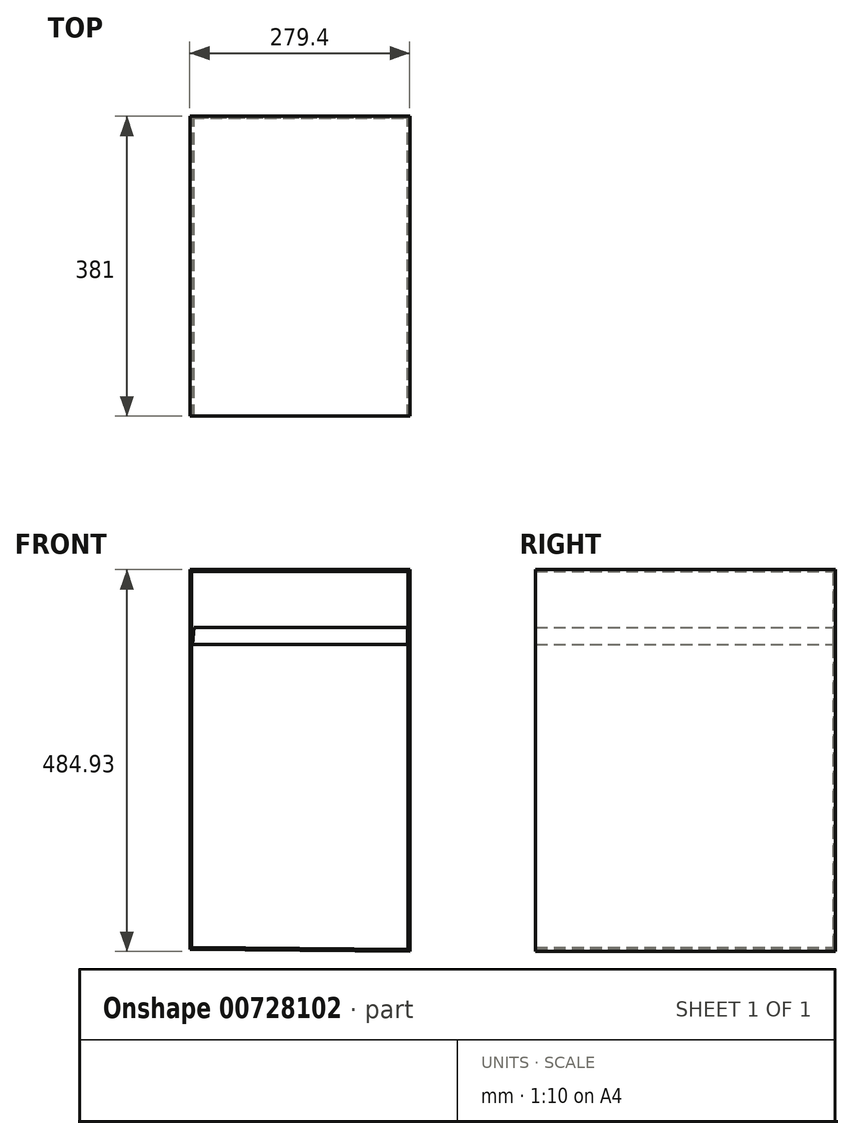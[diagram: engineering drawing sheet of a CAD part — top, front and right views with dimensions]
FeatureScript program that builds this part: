
annotation { "Feature Type Name" : "Feature", "Feature Type Description" : "" }
export const myFeature = defineFeature(function(context is Context, id is Id, definition is map)
    precondition{}
    {
        {
            var Q0;
            Q0=qCreatedBy(makeId("Front.planeOp"),FACE);
            var sketch = newSketch(context, id + "F0", { "sketchPlane" : qUnion([Q0])});
            skLineSegment(sketch, "E0", {"start": v(-49.26, 70.55) * mm, "end": v(-49.26, 553.15) * mm});
            skLineSegment(sketch, "E1", {"start": v(-49.26, 553.15) * mm, "end": v(230.14, 553.15) * mm});
            skLineSegment(sketch, "E2", {"start": v(230.14, 553.15) * mm, "end": v(230.14, 68.22) * mm});
            skLineSegment(sketch, "E3", {"start": v(230.14, 68.22) * mm, "end": v(-49.26, 70.55) * mm});
            skSolve(sketch);
        }
        {
            var Q0;
            Q0 = qSketchRegion(id + "F0", true);
            extrude(context, id + "F1", {"entities" : qUnion([Q0]), "depth" : 381 * mm, "offsetDistance" : 25.4 * mm});
        }
        {
            var Q0;
            Q0=makeQuery(id+"F1.opExtrude","CAP_FACE",FACE,{"disambiguationData":[OSD([sQuery(id+"F0.wireOp",EDGE,"E0"),sQuery(id+"F0.wireOp",EDGE,"E1"),sQuery(id+"F0.wireOp",EDGE,"E2"),sQuery(id+"F0.wireOp",EDGE,"E3")])],"isStart":false});
            shell(context, id + "F2", {"entities" : qUnion([Q0]), "thickness" : 2.54 * mm});
        }
        {
            var Q0;
            Q0=qCreatedBy(makeId("Front.planeOp"),FACE);
            var sketch = newSketch(context, id + "F3", { "sketchPlane" : qUnion([Q0])});
            skLineSegment(sketch, "E4", {"start": v(-43.76, 479.93) * mm, "end": v(227.3, 479.93) * mm});
            skLineSegment(sketch, "E5", {"start": v(227.3, 479.93) * mm, "end": v(227.3, 458.29) * mm});
            skLineSegment(sketch, "E6", {"start": v(227.3, 458.29) * mm, "end": v(-46.03, 458.29) * mm});
            skLineSegment(sketch, "E7", {"start": v(-46.03, 458.29) * mm, "end": v(-43.76, 479.93) * mm});
            skSolve(sketch);
        }
        {
            var Q0;
            Q0 = qSketchRegion(id + "F3", true);
            extrude(context, id + "F4", {"entities" : qUnion([Q0]), "operationType" : NewBodyOperationType.ADD, "depth" : 381 * mm, "offsetDistance" : 25.4 * mm});
        }
    });
